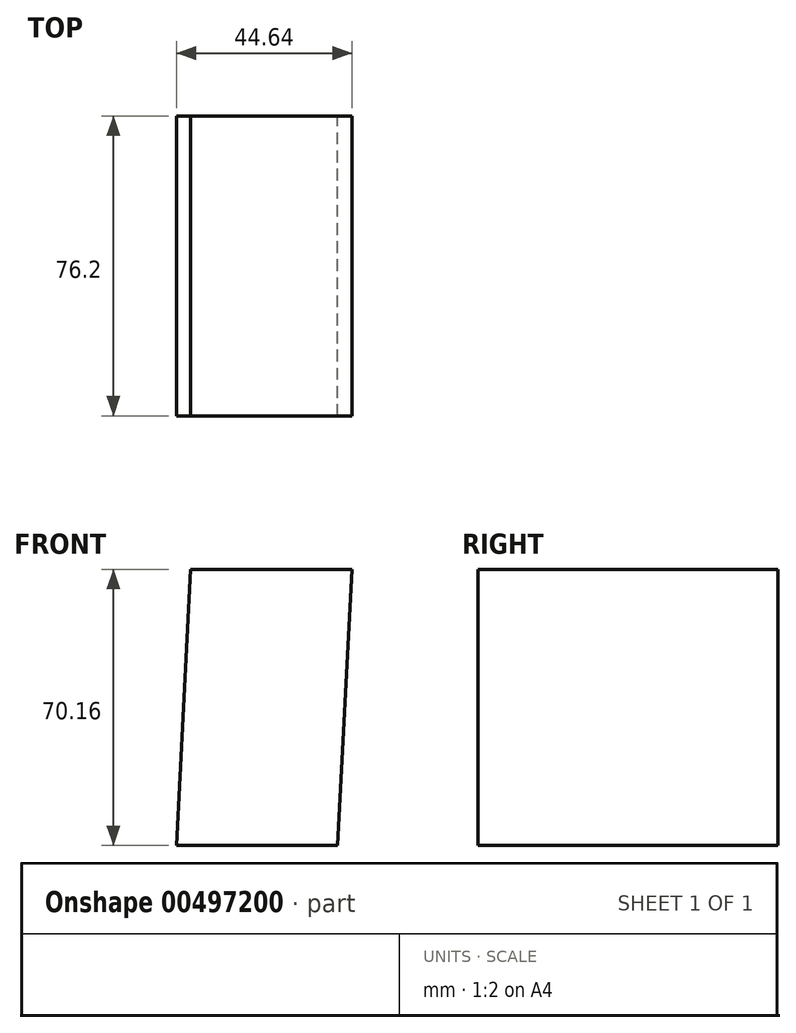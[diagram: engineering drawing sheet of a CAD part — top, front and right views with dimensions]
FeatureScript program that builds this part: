
annotation { "Feature Type Name" : "Feature", "Feature Type Description" : "" }
export const myFeature = defineFeature(function(context is Context, id is Id, definition is map)
    precondition{}
    {
        {
            var Q0;
            Q0=qCreatedBy(makeId("Front.planeOp"),FACE);
            var sketch = newSketch(context, id + "F0", { "sketchPlane" : qUnion([Q0])});
            skLineSegment(sketch, "E0.bottom", {"start": v(-18.04, 52.96) * mm, "end": v(22.92, 52.96) * mm});
            skLineSegment(sketch, "E0.top", {"start": v(-21.78, -17.2) * mm, "end": v(19.18, -17.2) * mm});
            skLineSegment(sketch, "E0.left", {"start": v(-18.04, 52.96) * mm, "end": v(-21.72, -17.2) * mm});
            skLineSegment(sketch, "E1", {"start": v(22.92, 52.96) * mm, "end": v(19.18, -17.2) * mm});
            skSolve(sketch);
        }
        {
            var Q0;
            Q0 = qSketchRegion(id + "F0", true);
            extrude(context, id + "F1", {"entities" : qUnion([Q0]), "depth" : 76.2 * mm});
        }
    });
